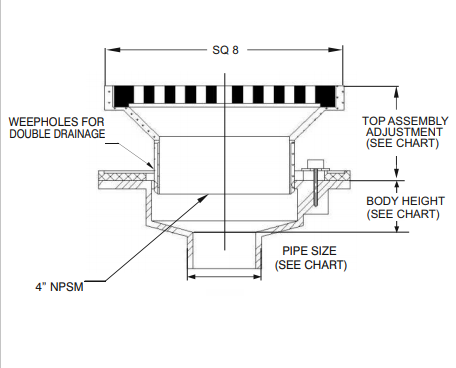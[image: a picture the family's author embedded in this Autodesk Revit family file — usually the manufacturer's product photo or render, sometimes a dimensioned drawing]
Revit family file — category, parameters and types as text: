
# Revit family: R1270-RG
name_source: partatom
category: Plumbing Fixtures
revit_build: Autodesk Revit 2018 (Build: 20170223_1515(x64)
units: mm (PartAtom-declared; Revit-internal decimal feet)

## family parameters
Cut with Voids When Loaded = No
Host = Face
Part Type = Normal
Room Calculation Point = No
Round Connector Dimension = Use Radius
Shared = No

## types (6) — shared parameters
Adjustmen Gap = 1' - 10 1/2"
Default Elevation = 0' - 0"
Description = COMBINED LARGE SUMP ROOF AND OVERFLOW DRAIN WITH DUCTILE IRON ROOFGUARD
Floor Drain Material = Paint - Sherwin Williams Paint - #952C2A - Bellwood Red
Galvanized Sump Receiver Length = 3' - 10"
Galvanized Sump Receiver Width = 2' - 0"
Manufacturer = MIFAB
Model = R1270-RG
URL = WWW.MIFAB.COM
zero-valued in all types: CWFU, WFU

## per-type parameters (varying)
| type | No Hub Standard Height | Pipe Diameter | Pipe Radius |
| 2" Drain Pipe Size | 0' - 6" | 0' - 2" | 0' - 1" |
| 3" Drain Pipe Size | 0' - 6" | 0' - 3" | 0' - 1 1/2" |
| 4" Drain Pipe Size | 0' - 6" | 0' - 4" | 0' - 2" |
| 5" Drain Pipe Size | 0' - 6" | 0' - 5" | 0' - 2 1/2" |
| 6" Drain Pipe Size | 0' - 7 1/2" | 0' - 6" | 0' - 3" |
| 8" Drain Pipe Size | 0' - 6" | 0' - 8" | 0' - 4" |

## geometry (parser evidence)
native form markers: Blend x7, Sweep x23
no freeform markers — native parametric forms only
